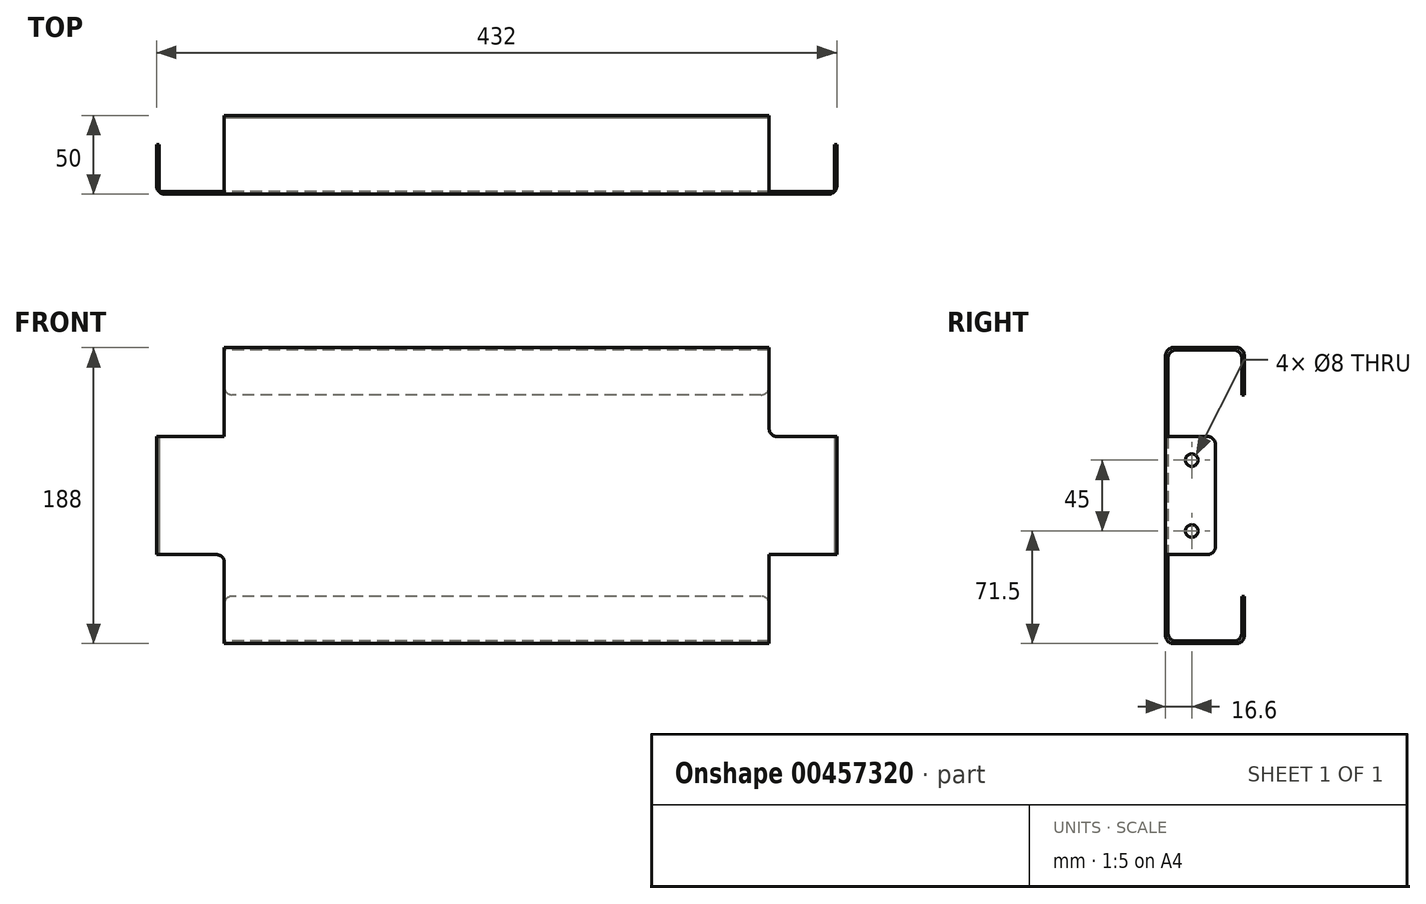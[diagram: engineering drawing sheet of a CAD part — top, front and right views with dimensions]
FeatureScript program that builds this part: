
annotation { "Feature Type Name" : "Feature", "Feature Type Description" : "" }
export const myFeature = defineFeature(function(context is Context, id is Id, definition is map)
    precondition{}
    {
        {
            var Q0;
            Q0=qCreatedBy(makeId("Right.planeOp"),FACE);
            var sketch = newSketch(context, id + "F0", { "sketchPlane" : qUnion([Q0])});
            skLineSegment(sketch, "E0", {"start": v(0, 0) * mm, "end": v(0, 94) * mm});
            skLineSegment(sketch, "E1", {"start": v(0, 94) * mm, "end": v(50, 94) * mm});
            skLineSegment(sketch, "E2", {"start": v(50, 94) * mm, "end": v(50, 64) * mm});
            skLineSegment(sketch, "E3", {"start": v(50, 64) * mm, "end": v(48.4, 64) * mm});
            skLineSegment(sketch, "E4", {"start": v(48.4, 64) * mm, "end": v(48.4, 92.4) * mm});
            skLineSegment(sketch, "E5", {"start": v(48.4, 92.4) * mm, "end": v(1.6, 92.4) * mm});
            skLineSegment(sketch, "E6", {"start": v(1.6, 92.4) * mm, "end": v(1.6, -92.4) * mm});
            skLineSegment(sketch, "E7", {"start": v(1.6, -92.4) * mm, "end": v(48.4, -92.4) * mm});
            skLineSegment(sketch, "E8", {"start": v(48.4, -92.4) * mm, "end": v(48.4, -64) * mm});
            skLineSegment(sketch, "E9", {"start": v(48.4, -64) * mm, "end": v(50, -64) * mm});
            skLineSegment(sketch, "E10", {"start": v(50, -64) * mm, "end": v(50, -94) * mm});
            skLineSegment(sketch, "E11", {"start": v(50, -94) * mm, "end": v(0, -94) * mm});
            skLineSegment(sketch, "E12", {"start": v(0, -94) * mm, "end": v(0, 0) * mm});
            skSolve(sketch);
        }
        {
            var Q0;
            Q0 = qSketchRegion(id + "F0", true);
            extrude(context, id + "F1", {"entities" : qUnion([Q0]), "endBound" : BoundingType.SYMMETRIC, "depth" : 346 * mm});
        }
        {
            var Q0;
            Q0=makeQuery(id+"F1.opExtrude","CAP_FACE",FACE,{"disambiguationData":[OSD([sQuery(id+"F0.wireOp",EDGE,"E0"),sQuery(id+"F0.wireOp",EDGE,"E1"),sQuery(id+"F0.wireOp",EDGE,"E2"),sQuery(id+"F0.wireOp",EDGE,"E3"),sQuery(id+"F0.wireOp",EDGE,"E4"),sQuery(id+"F0.wireOp",EDGE,"E5"),sQuery(id+"F0.wireOp",EDGE,"E6"),sQuery(id+"F0.wireOp",EDGE,"E7"),sQuery(id+"F0.wireOp",EDGE,"E8"),sQuery(id+"F0.wireOp",EDGE,"E9"),sQuery(id+"F0.wireOp",EDGE,"E10"),sQuery(id+"F0.wireOp",EDGE,"E11"),sQuery(id+"F0.wireOp",EDGE,"E12")])],"isStart":false});
            var sketch = newSketch(context, id + "F2", { "sketchPlane" : qUnion([Q0])});
            skLineSegment(sketch, "E13", {"start": v(0, 0) * mm, "end": v(0, 37.5) * mm});
            skLineSegment(sketch, "E14", {"start": v(0, 37.5) * mm, "end": v(1.6, 37.5) * mm});
            skLineSegment(sketch, "E15", {"start": v(1.6, 37.5) * mm, "end": v(1.6, -37.5) * mm});
            skLineSegment(sketch, "E16", {"start": v(1.6, -37.5) * mm, "end": v(0, -37.5) * mm});
            skLineSegment(sketch, "E17", {"start": v(0, -37.5) * mm, "end": v(0, 0) * mm});
            skSolve(sketch);
        }
        {
            var Q0;
            Q0 = qSketchRegion(id + "F2", true);
            extrude(context, id + "F3", {"entities" : qUnion([Q0]), "operationType" : NewBodyOperationType.ADD, "depth" : 43 * mm});
        }
        {
            var Q0;
            Q0=makeQuery(id+"F1.opExtrude","CAP_FACE",FACE,{"disambiguationData":[OSD([sQuery(id+"F0.wireOp",EDGE,"E0"),sQuery(id+"F0.wireOp",EDGE,"E1"),sQuery(id+"F0.wireOp",EDGE,"E2"),sQuery(id+"F0.wireOp",EDGE,"E3"),sQuery(id+"F0.wireOp",EDGE,"E4"),sQuery(id+"F0.wireOp",EDGE,"E5"),sQuery(id+"F0.wireOp",EDGE,"E6"),sQuery(id+"F0.wireOp",EDGE,"E7"),sQuery(id+"F0.wireOp",EDGE,"E8"),sQuery(id+"F0.wireOp",EDGE,"E9"),sQuery(id+"F0.wireOp",EDGE,"E10"),sQuery(id+"F0.wireOp",EDGE,"E11"),sQuery(id+"F0.wireOp",EDGE,"E12")])],"isStart":true});
            var sketch = newSketch(context, id + "F4", { "sketchPlane" : qUnion([Q0])});
            skLineSegment(sketch, "E18", {"start": v(0, 0) * mm, "end": v(0, 37.5) * mm});
            skLineSegment(sketch, "E19", {"start": v(0, 37.5) * mm, "end": v(-1.6, 37.5) * mm});
            skLineSegment(sketch, "E20", {"start": v(-1.6, 37.5) * mm, "end": v(-1.6, -37.5) * mm});
            skLineSegment(sketch, "E21", {"start": v(-1.6, -37.5) * mm, "end": v(0, -37.5) * mm});
            skLineSegment(sketch, "E22", {"start": v(0, -37.5) * mm, "end": v(0, 0) * mm});
            skSolve(sketch);
        }
        {
            var Q0;
            Q0 = qSketchRegion(id + "F4", true);
            extrude(context, id + "F5", {"entities" : qUnion([Q0]), "operationType" : NewBodyOperationType.ADD, "depth" : 43 * mm});
        }
        {
            var Q0;
            Q0=makeQuery(id+"F5.boolean.opBoolean","MERGE",FACE,{"derivedFrom":[makeQuery(id+"F3.boolean.opBoolean","MERGE",FACE,{"derivedFrom":[makeQuery(id+"F1.opExtrude","SWEPT_FACE",FACE,{"disambiguationData":[OSD([sQuery(id+"F0.wireOp",EDGE,"E6")])]}),makeQuery(id+"F3.opExtrude","SWEPT_FACE",FACE,{"disambiguationData":[OSD([sQuery(id+"F2.wireOp",EDGE,"E15")])]})]}),makeQuery(id+"F5.opExtrude","SWEPT_FACE",FACE,{"disambiguationData":[OSD([sQuery(id+"F4.wireOp",EDGE,"E20")])]})]});
            var sketch = newSketch(context, id + "F6", { "sketchPlane" : qUnion([Q0])});
            skLineSegment(sketch, "E23", {"start": v(-216, 37.5) * mm, "end": v(-214.4, 37.5) * mm});
            skLineSegment(sketch, "E24", {"start": v(-214.4, 37.5) * mm, "end": v(-214.4, -37.5) * mm});
            skLineSegment(sketch, "E25", {"start": v(-214.4, -37.5) * mm, "end": v(-216, -37.5) * mm});
            skLineSegment(sketch, "E26", {"start": v(-216, -37.5) * mm, "end": v(-216, 37.5) * mm});
            skLineSegment(sketch, "E27", {"start": v(216, 37.5) * mm, "end": v(214.4, 37.5) * mm});
            skLineSegment(sketch, "E28", {"start": v(214.4, 37.5) * mm, "end": v(214.4, -37.5) * mm});
            skLineSegment(sketch, "E29", {"start": v(214.4, -37.5) * mm, "end": v(216, -37.5) * mm});
            skLineSegment(sketch, "E30", {"start": v(216, -37.5) * mm, "end": v(216, 37.5) * mm});
            skSolve(sketch);
        }
        {
            var Q0;
            Q0 = qSketchRegion(id + "F6", true);
            extrude(context, id + "F7", {"entities" : qUnion([Q0]), "operationType" : NewBodyOperationType.ADD, "depth" : 30 * mm});
        }
        {
            var Q0;
            Q0=makeQuery(id+"F7.boolean.opBoolean","MERGE",FACE,{"derivedFrom":[makeQuery(id+"F3.opExtrude","CAP_FACE",FACE,{"disambiguationData":[OSD([sQuery(id+"F2.wireOp",EDGE,"E13"),sQuery(id+"F2.wireOp",EDGE,"E14"),sQuery(id+"F2.wireOp",EDGE,"E15"),sQuery(id+"F2.wireOp",EDGE,"E16"),sQuery(id+"F2.wireOp",EDGE,"E17")])],"isStart":false}),makeQuery(id+"F7.opExtrude","SWEPT_FACE",FACE,{"disambiguationData":[OSD([sQuery(id+"F6.wireOp",EDGE,"E26")])]})]});
            var sketch = newSketch(context, id + "F8", { "sketchPlane" : qUnion([Q0])});
            skCircle(sketch, "E31", {"center": v(16.6, 22.5) * mm, "radius": 4 * mm});
            skCircle(sketch, "E32", {"center": v(16.6, -22.5) * mm, "radius": 4 * mm});
            skSolve(sketch);
        }
        {
            var Q0;
            Q0 = qSketchRegion(id + "F8", true);
            extrude(context, id + "F9", {"entities" : qUnion([Q0]), "operationType" : NewBodyOperationType.REMOVE, "endBound" : BoundingType.THROUGH_ALL, "oppositeDirection" : true, "depth" : 25 * mm});
        }
        {
            var Q0;
            Q0=makeQuery(id+"F3.opExtrude","CAP_EDGE",EDGE,{"disambiguationData":[OSD([sQuery(id+"F2.wireOp",EDGE,"E14")])],"isStart":true});
            var Q1;
            Q1=makeQuery(id+"F7.opExtrude","CAP_EDGE",EDGE,{"disambiguationData":[OSD([sQuery(id+"F6.wireOp",EDGE,"E25")])],"isStart":false});
            var Q2;
            Q2=makeQuery(id+"F3.opExtrude","CAP_EDGE",EDGE,{"disambiguationData":[OSD([sQuery(id+"F2.wireOp",EDGE,"E16")])],"isStart":true});
            var Q3;
            Q3=makeQuery(id+"F1.opExtrude","CAP_EDGE",EDGE,{"disambiguationData":[OSD([sQuery(id+"F0.wireOp",EDGE,"E3")])],"isStart":false});
            var Q4;
            Q4=makeQuery(id+"F1.opExtrude","CAP_EDGE",EDGE,{"disambiguationData":[OSD([sQuery(id+"F0.wireOp",EDGE,"E9")])],"isStart":false});
            var Q5;
            Q5=makeQuery(id+"F7.opExtrude","CAP_EDGE",EDGE,{"disambiguationData":[OSD([sQuery(id+"F6.wireOp",EDGE,"E23")])],"isStart":false});
            var Q6;
            Q6=makeQuery(id+"F1.opExtrude","CAP_EDGE",EDGE,{"disambiguationData":[OSD([sQuery(id+"F0.wireOp",EDGE,"E9")])],"isStart":true});
            var Q7;
            Q7=makeQuery(id+"F5.opExtrude","CAP_EDGE",EDGE,{"disambiguationData":[OSD([sQuery(id+"F4.wireOp",EDGE,"E21")])],"isStart":true});
            var Q8;
            Q8=makeQuery(id+"F7.opExtrude","CAP_EDGE",EDGE,{"disambiguationData":[OSD([sQuery(id+"F6.wireOp",EDGE,"E29")])],"isStart":false});
            var Q9;
            Q9=makeQuery(id+"F7.opExtrude","CAP_EDGE",EDGE,{"disambiguationData":[OSD([sQuery(id+"F6.wireOp",EDGE,"E27")])],"isStart":false});
            var Q10;
            Q10=makeQuery(id+"F5.opExtrude","CAP_EDGE",EDGE,{"disambiguationData":[OSD([sQuery(id+"F4.wireOp",EDGE,"E19")])],"isStart":true});
            var Q11;
            Q11=makeQuery(id+"F1.opExtrude","CAP_EDGE",EDGE,{"disambiguationData":[OSD([sQuery(id+"F0.wireOp",EDGE,"E3")])],"isStart":true});
            var Q12;
            Q12=makeQuery(id+"F1.opExtrude","SWEPT_EDGE",EDGE,{"disambiguationData":[OSD([sQuery(id+"F0.wireOp",EDGE,"E10"),sQuery(id+"F0.wireOp",EDGE,"E11")])]});
            var Q13;
            Q13=makeQuery(id+"F1.opExtrude","SWEPT_EDGE",EDGE,{"disambiguationData":[OSD([sQuery(id+"F0.wireOp",EDGE,"E11"),sQuery(id+"F0.wireOp",EDGE,"E12")])]});
            var Q14;
            Q14=makeQuery(id+"F5.opExtrude","CAP_EDGE",EDGE,{"disambiguationData":[OSD([sQuery(id+"F4.wireOp",EDGE,"E18"),sQuery(id+"F4.wireOp",EDGE,"E22")])],"isStart":false});
            var Q15;
            Q15=makeQuery(id+"F1.opExtrude","SWEPT_EDGE",EDGE,{"disambiguationData":[OSD([sQuery(id+"F0.wireOp",EDGE,"E6"),sQuery(id+"F0.wireOp",EDGE,"E7")])]});
            var Q16;
            Q16=makeQuery(id+"F1.opExtrude","SWEPT_EDGE",EDGE,{"disambiguationData":[OSD([sQuery(id+"F0.wireOp",EDGE,"E7"),sQuery(id+"F0.wireOp",EDGE,"E8")])]});
            var Q17;
            Q17=makeQuery(id+"F7.opExtrude","CAP_EDGE",EDGE,{"disambiguationData":[OSD([sQuery(id+"F6.wireOp",EDGE,"E28")])],"isStart":true});
            var Q18;
            Q18=makeQuery(id+"F7.opExtrude","CAP_EDGE",EDGE,{"disambiguationData":[OSD([sQuery(id+"F6.wireOp",EDGE,"E24")])],"isStart":true});
            var Q19;
            Q19=makeQuery(id+"F3.opExtrude","CAP_EDGE",EDGE,{"disambiguationData":[OSD([sQuery(id+"F2.wireOp",EDGE,"E13"),sQuery(id+"F2.wireOp",EDGE,"E17")])],"isStart":false});
            var Q20;
            Q20=makeQuery(id+"F1.opExtrude","SWEPT_EDGE",EDGE,{"disambiguationData":[OSD([sQuery(id+"F0.wireOp",EDGE,"E0"),sQuery(id+"F0.wireOp",EDGE,"E1")])]});
            var Q21;
            Q21=makeQuery(id+"F1.opExtrude","SWEPT_EDGE",EDGE,{"disambiguationData":[OSD([sQuery(id+"F0.wireOp",EDGE,"E1"),sQuery(id+"F0.wireOp",EDGE,"E2")])]});
            var Q22;
            Q22=makeQuery(id+"F1.opExtrude","SWEPT_EDGE",EDGE,{"disambiguationData":[OSD([sQuery(id+"F0.wireOp",EDGE,"E4"),sQuery(id+"F0.wireOp",EDGE,"E5")])]});
            var Q23;
            Q23=makeQuery(id+"F1.opExtrude","SWEPT_EDGE",EDGE,{"disambiguationData":[OSD([sQuery(id+"F0.wireOp",EDGE,"E5"),sQuery(id+"F0.wireOp",EDGE,"E6")])]});
            fillet(context, id + "F10", {"entities" : qUnion([Q0, Q1, Q2, Q3, Q4, Q5, Q6, Q7, Q8, Q9, Q10, Q11, Q12, Q13, Q14, Q15, Q16, Q17, Q18, Q19, Q20, Q21, Q22, Q23]), "radius" : 5 * mm, "tangentPropagation" : true, "allowEdgeOverflow" : false});
        }
    });
